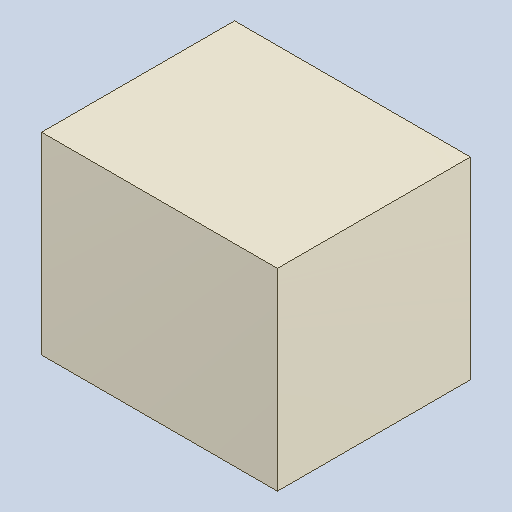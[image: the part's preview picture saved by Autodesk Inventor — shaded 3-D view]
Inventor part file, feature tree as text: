
AUTODESK INVENTOR PART (.ipt)
format: ipt  version: 2023.4 (Build 274418000, 418)  size: 81,920 bytes
history: native  units: mm
features: extrude x1
ambient origin geometry x8: Origin, YZ Plane, XZ Plane, XY Plane, X Axis, Y Axis, Z Axis, Center Point
bodies: Solid1 (feature_tree)
feature tree (1):
  extrude  "Extruded_6"  [1 undecoded]
note: 1 required parameter value undecoded (feature->parameter linkage not recoverable at this tier; creation-order binding heuristic only, values carry confidence <= 0.55)
